# Revit family: Gira_2021112
name_source: partatom
category: Elektroinstallationen
revit_build: Autodesk Revit 2017 (Build: 20160225_1515(x64)
units: mm (PartAtom-declared; Revit-internal decimal feet)

## family parameters
Basisbauteil = Fläche
Beim Laden mit Abzugskörper schneiden = Nein
Bemaßung runder Anschluss = Durchmesser verwenden
Beschriftungsausrichtung beibehalten = Nein
Gemeinsam genutzt = Nein
Raumberechnungspunkt = Nein
Teiletyp = Normal

## types (1)
- KNX Tastsens.3 Basis 1f Flächenschalter Reinweiß
    Andere Bussysteme = ohne
    Anzahl der Betätigungspunkte = 2
    Anzahl der Tasten = 1
    Ausführung der Oberfläche = glänzend
    BIM = https://media.stage.bim.site Tastsensor 3 Komfort 1fach.rfa
    BIMSITE_PRODUCT_ID = eac69390b908ca6ac66c86d50474756653b7384d
    Beschreibung = KNX Tastsensor 3 Basis 1fach  Reinweiß glänzend Merkmale:  Montage auf Busankoppler 3.  Demontageschutz durch Verschraubung.  Wippenfunktion: Schalten, Dimmen, Jalousie, Wertgeber 1 Byte und Szenennebenstelle.  Zwei blaue Status-LEDs je Bedienfläche.  Weiße Betriebs-LED.  Funktion der Betriebs-LED und der Status-LED parametrierbar.  Hinweise :  Professionelle Beschriftung über den Gira Beschriftungsservice www.beschriftung.gira.de.
    Bussystem Funkbus = Nein
    Bussystem KNX = Ja
    Bussystem KNX-Funk = Nein
    Bussystem LON = Nein
    Bussystem Powernet = Nein
    Datenblatt = https://media.stage.bim.site
    Datenblatt 1 = https://media.stage.bim.site
    Farbe = weiß
    GTIN = 4010337081661
    HAN = 2021112
    HeinzeBIM = https://www.heinze.de
    Hersteller = Gira
    Kosten = 0 $
    Mit Beschriftungsfeld = Nein
    Mit Busankopplung = Nein
    Mit Diebstahl-/Demontageschutz = Ja
    Mit Display = Nein
    Mit Infrarotsensor = Nein
    Mit LED-Anzeige = Ja
    Mit Raumthermostat = Nein
    Montageart = Unterputz
    Oberfläche Text = sonstige
    Produktseite = https://media.stage.bim.site
    RAL-Nummer (ähnlich) = 9010
    Schutzart (IP) = IP20
    Transparent = Nein
    Typname = KNX Tastsens.3 Basis 1f Flächenschalter Reinweiß
    URL = https://www.gira.de
    Vorgabe-Ansicht = 1219 mm
    Werkstoff Text = Kunststoff
    Werkstoffgüte = Thermoplast

## geometry (parser evidence)
native form markers: Sweep x2
no freeform markers — native parametric forms only
